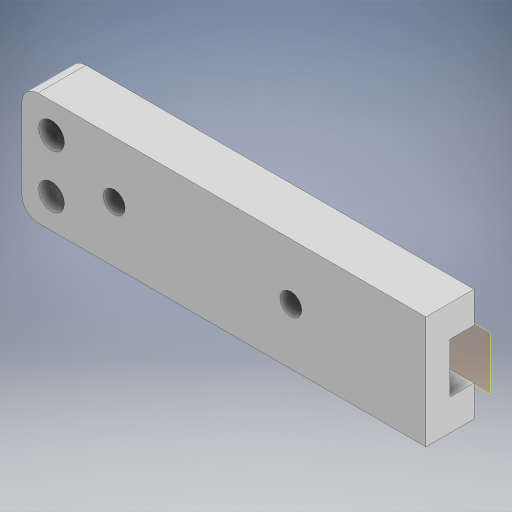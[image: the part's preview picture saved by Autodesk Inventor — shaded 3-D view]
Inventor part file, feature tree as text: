
AUTODESK INVENTOR PART (.ipt)
format: ipt  version: 2024 (Build 280153000, 153)  size: 306,688 bytes
history: native  units: mm
features: other x7, sketch x4, projected_geometry x4, extrude x3, reference x2, hole x1, fillet x1
ambient origin geometry x8: Origin, YZ Plane, XZ Plane, XY Plane, X Axis, Y Axis, Z Axis, Center Point
bodies: Body1 (feature_tree)
feature tree (22):
  other  "솔리드1"
  other  "작업 평면1"
  extrude  "돌출1"  Depth=0.3mm
  extrude  "돌출2"  Depth=4.0mm
  hole  "구멍1"  [1 undecoded]
  fillet  "모깎기1"  Radius=3.0mm
  other  "직접 편집1"
  extrude  "돌출3"  Depth=2.0mm
  sketch  "스케치1"
  reference  "참조1"
  sketch  "스케치2"
  projected_geometry  "투영된 루프1"
  reference  "참조2"
  sketch  "스케치3"
  projected_geometry  "투영된 루프2"
  sketch  "스케치4"
  projected_geometry  "투영된 루프3"
  projected_geometry  "투영된 루프4"
  other  "<userpath>\Desktop\ZIG\조립품1.iam"
  other  "조립품1.iam"
  other  "body_ver2:1"
  other  "이동1"
note: 1 required parameter value undecoded (feature->parameter linkage not recoverable at this tier; creation-order binding heuristic only, values carry confidence <= 0.55)
